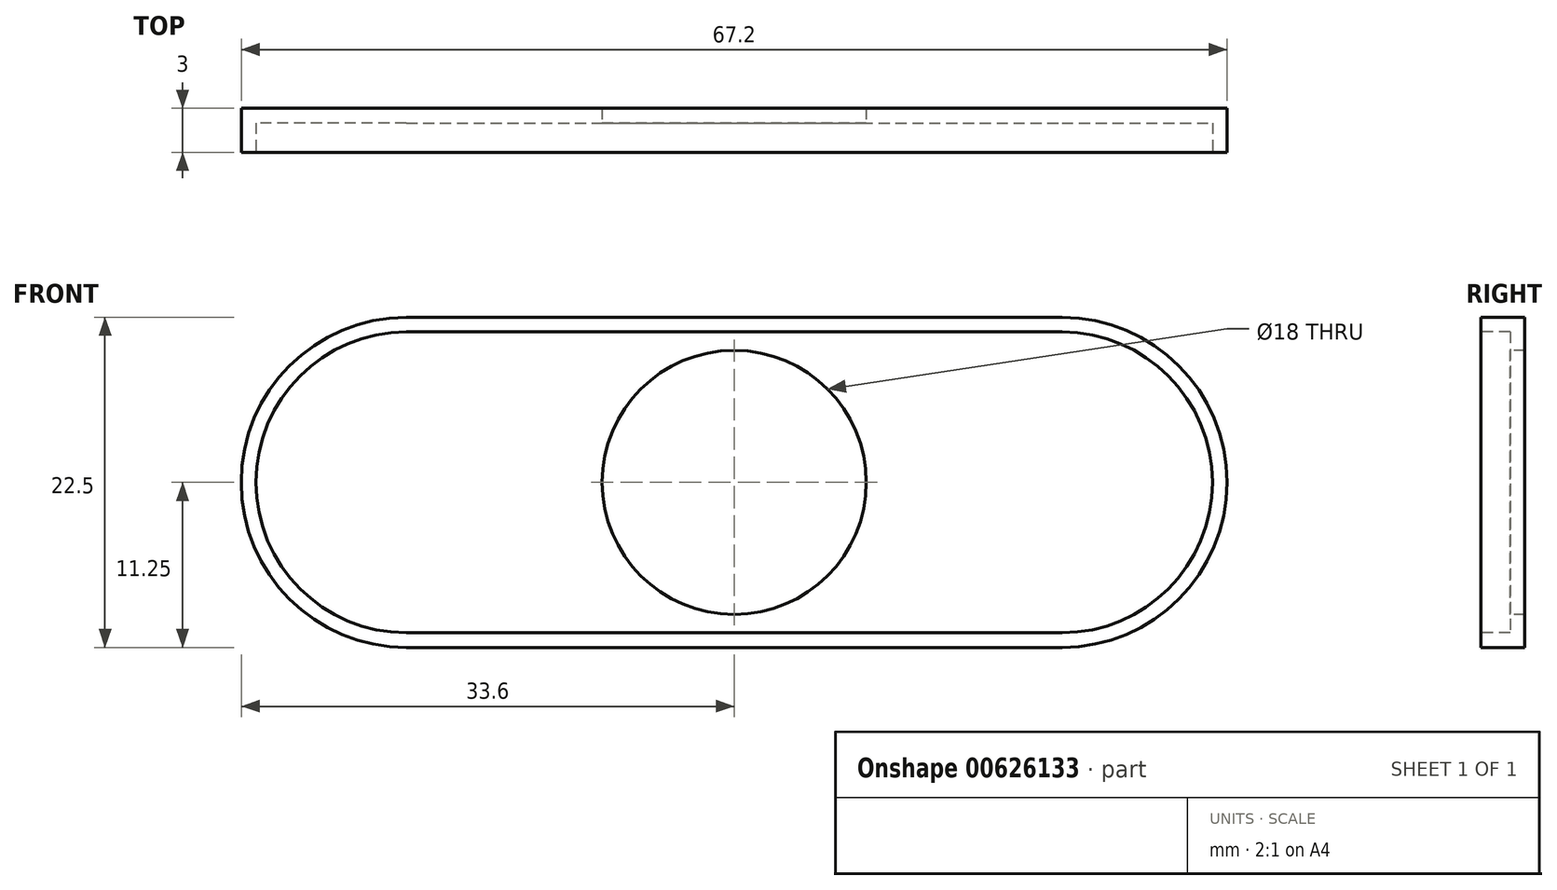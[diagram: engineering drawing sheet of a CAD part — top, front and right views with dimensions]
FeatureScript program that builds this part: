
annotation { "Feature Type Name" : "Feature", "Feature Type Description" : "" }
export const myFeature = defineFeature(function(context is Context, id is Id, definition is map)
    precondition{}
    {
        {
            var Q0;
            Q0=qCreatedBy(makeId("Front.planeOp"),FACE);
            var sketch = newSketch(context, id + "F0", { "sketchPlane" : qUnion([Q0])});
            skLineSegment(sketch, "E0.bottom", {"start": v(22.35, -11.25) * mm, "end": v(-22.35, -11.25) * mm});
            skLineSegment(sketch, "E0.top", {"start": v(22.35, 11.25) * mm, "end": v(-22.35, 11.25) * mm});
            skPoint(sketch, "E0.middle", {"position": v(0, 0) * mm});
            skArc(sketch, "E1", {"start": v(-22.35, 11.25) * mm, "mid": v(-33.6, 0) * mm, "end": v(-22.35, -11.25) * mm});
            skArc(sketch, "E2", {"start": v(22.35, -11.25) * mm, "mid": v(33.6, 0) * mm, "end": v(22.35, 11.25) * mm});
            skSolve(sketch);
        }
        {
            var Q0;
            Q0=makeQuery(id+"F0.imprint","IMPRINT",FACE,{"disambiguationData":[TD([[makeQuery(id+"F0.imprint","IMPRINT",EDGE,{"derivedFrom":sQuery(id+"F0.wireOp",EDGE,"E0.bottom")}),-1.0]])]});
            extrude(context, id + "F1", {"entities" : qUnion([Q0]), "depth" : 3 * mm, "offsetDistance" : 25 * mm});
        }
        {
            var Q0;
            Q0=makeQuery(id+"F1.opExtrude","CAP_FACE",FACE,{"disambiguationData":[OSD([sQuery(id+"F0.wireOp",EDGE,"E0.bottom"),sQuery(id+"F0.wireOp",EDGE,"E0.top"),sQuery(id+"F0.wireOp",EDGE,"E1"),sQuery(id+"F0.wireOp",EDGE,"E2")])],"isStart":false});
            var sketch = newSketch(context, id + "F2", { "sketchPlane" : qUnion([Q0])});
            skArc(sketch, "E3", {"start": v(-22.35, 10.25) * mm, "mid": v(-32.6, 0) * mm, "end": v(-22.35, -10.25) * mm});
            skArc(sketch, "E4", {"start": v(22.35, -10.25) * mm, "mid": v(32.6, 0) * mm, "end": v(22.35, 10.25) * mm});
            skLineSegment(sketch, "E5", {"start": v(-22.35, 10.25) * mm, "end": v(22.35, 10.25) * mm});
            skLineSegment(sketch, "E6", {"start": v(-22.35, -10.25) * mm, "end": v(22.35, -10.25) * mm});
            skSolve(sketch);
        }
        {
            var Q0;
            Q0=makeQuery(id+"F2.imprint","IMPRINT",FACE,{"disambiguationData":[TD([[makeQuery(id+"F2.imprint","IMPRINT",EDGE,{"derivedFrom":sQuery(id+"F2.wireOp",EDGE,"E3")}),1.0]])]});
            extrude(context, id + "F3", {"entities" : qUnion([Q0]), "operationType" : NewBodyOperationType.REMOVE, "oppositeDirection" : true, "depth" : 2 * mm, "offsetDistance" : 25 * mm});
        }
        {
            var Q0;
            Q0=makeQuery(id+"F3.boolean.opBoolean","COPY",FACE,{"derivedFrom":makeQuery(id+"F3.opExtrude","CAP_FACE",FACE,{"disambiguationData":[OSD([sQuery(id+"F2.wireOp",EDGE,"E3"),sQuery(id+"F2.wireOp",EDGE,"E4"),sQuery(id+"F2.wireOp",EDGE,"E5"),sQuery(id+"F2.wireOp",EDGE,"E6")])],"isStart":false})});
            var sketch = newSketch(context, id + "F4", { "sketchPlane" : qUnion([Q0])});
            skCircle(sketch, "E7", {"center": v(0, 0) * mm, "radius": 9 * mm});
            skSolve(sketch);
        }
        {
            var Q0;
            Q0=makeQuery(id+"F4.imprint","IMPRINT",FACE,{"disambiguationData":[TD([[makeQuery(id+"F4.imprint","IMPRINT",EDGE,{"derivedFrom":sQuery(id+"F4.wireOp",EDGE,"E7")}),1.0]])]});
            extrude(context, id + "F5", {"entities" : qUnion([Q0]), "operationType" : NewBodyOperationType.REMOVE, "endBound" : BoundingType.THROUGH_ALL, "oppositeDirection" : true, "depth" : 25 * mm, "offsetDistance" : 25 * mm});
        }
        {
            var Q0;
            Q0=makeQuery(id+"F1.opExtrude","CAP_FACE",FACE,{"disambiguationData":[OSD([sQuery(id+"F0.wireOp",EDGE,"E0.bottom"),sQuery(id+"F0.wireOp",EDGE,"E0.top"),sQuery(id+"F0.wireOp",EDGE,"E1"),sQuery(id+"F0.wireOp",EDGE,"E2")])],"isStart":true});
            var sketch = newSketch(context, id + "F6", { "sketchPlane" : qUnion([Q0])});
            skCircle(sketch, "E8", {"center": v(0, 0) * mm, "radius": 9 * mm});
            skArc(sketch, "E9.0.0", {"start": v(-22.35, 11.25) * mm, "mid": v(-33.6, 0) * mm, "end": v(-22.35, -11.25) * mm});
            skLineSegment(sketch, "E9.0.1", {"start": v(-22.35, -11.25) * mm, "end": v(22.35, -11.25) * mm});
            skArc(sketch, "E9.0.2", {"start": v(22.35, -11.25) * mm, "mid": v(33.6, 0) * mm, "end": v(22.35, 11.25) * mm});
            skLineSegment(sketch, "E9.0.3", {"start": v(22.35, 11.25) * mm, "end": v(-22.35, 11.25) * mm});
            skSolve(sketch);
        }
        {
            var Q0;
            Q0=makeQuery(id+"F6.imprint","IMPRINT",FACE,{"disambiguationData":[TD([[makeQuery(id+"F6.imprint","IMPRINT",EDGE,{"derivedFrom":sQuery(id+"F6.wireOp",EDGE,"E8")}),-1.0]])]});
            var Q1;
            Q1=sQuery(id+"F6.wireOp",EDGE,"E8");
            extrude(context, id + "F7", {"entities" : qUnion([Q0]), "bodyType" : ToolBodyType.SURFACE, "operationType" : NewBodyOperationType.ADD, "surfaceEntities" : qUnion([Q1]), "depth" : 1 * mm, "offsetDistance" : 25 * mm});
        }
    });
